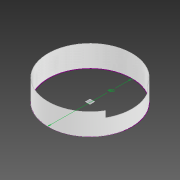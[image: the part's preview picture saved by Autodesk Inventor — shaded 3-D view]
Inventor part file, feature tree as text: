
AUTODESK INVENTOR PART (.ipt)
format: ipt  version: 2020 (Build 240168000, 168)  size: 212,992 bytes
history: native  units: in
note: dims shown in document units (in); Inventor stores cm internally (conversion verified against a paired STEP export)
features: sketch x6, extrude x5, plane x4
ambient origin geometry x8: Origin, YZ Plane, XZ Plane, XY Plane, X Axis, Y Axis, Z Axis, Center Point
bodies: Solid1 (feature_tree)
feature tree (15):
  sketch  "Sketch1"  dims[d0=15.748in d3=5.0in]
  plane  "Work Plane1"
  extrude  "Extrusion2"  Depth=5.0in
  plane  "Work Plane4"
  extrude  "Extrusion3"  Depth=0.1181in TaperAngle=0.0deg
  plane  "Work Plane2"
  extrude  "Extrusion4"  Depth=1.1811in
  plane  "Work Plane3"
  extrude  "Extrusion5"  Depth=0.1969in
  extrude  "Extrusion6"  Depth=0.6693in
  sketch  "Sketch2"  dims[d4=11.2992in d5=0.1181in d6=0.0in]
  sketch  "Sketch3"  dims[d7=2.3622in d8=1.1811in]
  sketch  "Sketch4"  dims[d9=1.0236in d10=0.1969in]
  sketch  "Sketch5"  dims[d11=7.0866in d13=360.0deg d15=0.6693in]
  sketch  "Sketch6"  dims[d16=0.3937in d18=0.1575in d19=0.1181in d20=7.0866in d22=360.0deg d24=3.937in d26=360.0deg d28=0.1181in d29=0.0in d30=6.6929in d31=13.3858in d32=1.5748in d33=0.9843in d34=2.5591in d35=2.5591in d36=2.5591in d37=2.5591in d38=2.5591in d39=0.1181in d40=0.1181in d41=0.1181in d42=0.1181in d43=0.3937in d44=0.0in d45=15.8268in d46=15.748in d47=3.937in d48=0.1181in d49=0.0in d50=0.0in d51=2.3622in d52=7.874in d53=11.811in d54=0.0in]
